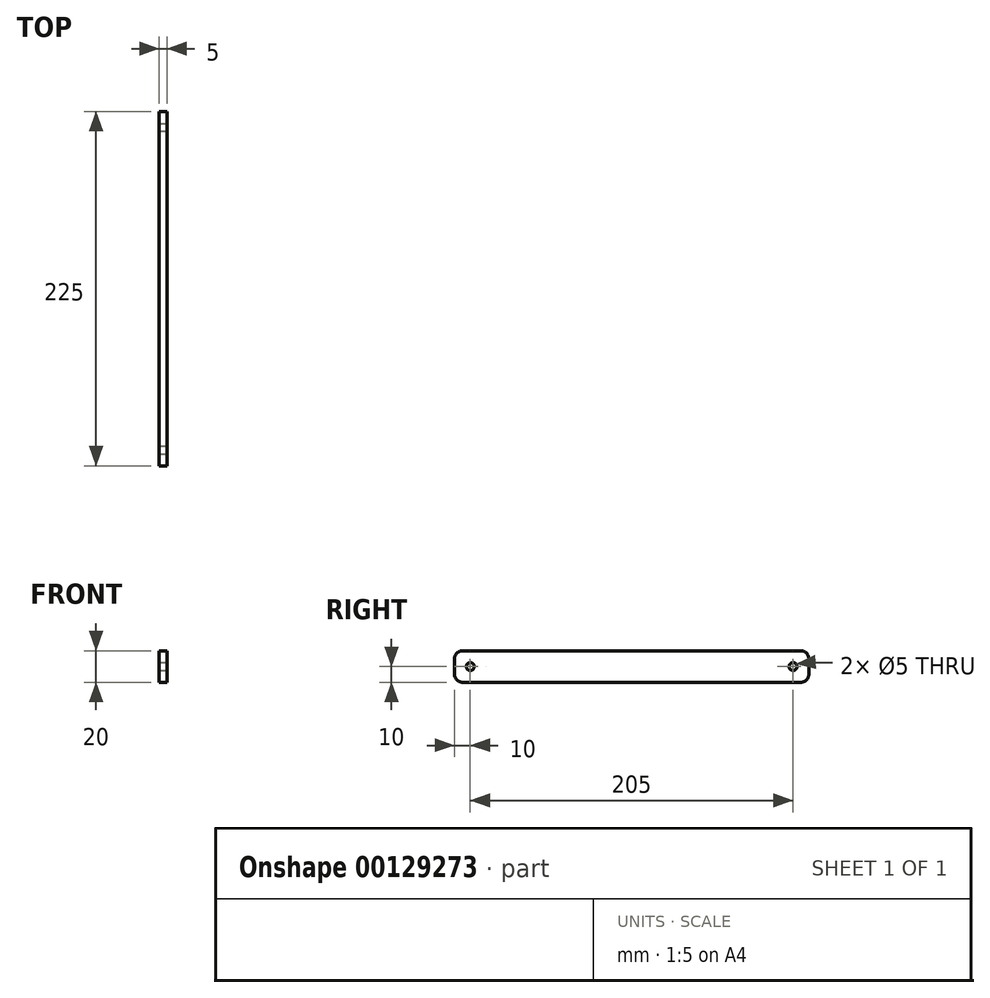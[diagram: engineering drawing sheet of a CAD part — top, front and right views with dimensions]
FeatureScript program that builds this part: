
annotation { "Feature Type Name" : "Feature", "Feature Type Description" : "" }
export const myFeature = defineFeature(function(context is Context, id is Id, definition is map)
    precondition{}
    {
        {
            var Q0;
            Q0=qCreatedBy(makeId("Right.planeOp"),FACE);
            var sketch = newSketch(context, id + "F0", { "sketchPlane" : qUnion([Q0])});
            skLineSegment(sketch, "E0.bottom", {"start": v(0, 0) * mm, "end": v(225, 0) * mm});
            skLineSegment(sketch, "E0.top", {"start": v(0, 20) * mm, "end": v(225, 20) * mm});
            skLineSegment(sketch, "E0.left", {"start": v(0, 0) * mm, "end": v(0, 20) * mm});
            skLineSegment(sketch, "E0.right", {"start": v(225, 0) * mm, "end": v(225, 20) * mm});
            skCircle(sketch, "E1", {"center": v(10, 10) * mm, "radius": 2.5 * mm});
            skPoint(sketch, "E1.centerSnap0", {"position": v(0, 10) * mm});
            skCircle(sketch, "E2", {"center": v(215, 10) * mm, "radius": 2.5 * mm});
            skSolve(sketch);
        }
        {
            var Q0;
            Q0=makeQuery(id+"F0.imprint","IMPRINT",FACE,{"disambiguationData":[TD([[makeQuery(id+"F0.imprint","IMPRINT",EDGE,{"derivedFrom":sQuery(id+"F0.wireOp",EDGE,"E0.bottom")}),1.0]])]});
            extrude(context, id + "F1", {"entities" : qUnion([Q0]), "oppositeDirection" : true, "depth" : 5 * mm});
        }
        {
            var Q0;
            Q0=makeQuery(id+"F1.opExtrude","SWEPT_EDGE",EDGE,{"disambiguationData":[OSD([sQuery(id+"F0.wireOp",EDGE,"E0.top"),sQuery(id+"F0.wireOp",EDGE,"E0.left")])]});
            var Q1;
            Q1=makeQuery(id+"F1.opExtrude","SWEPT_EDGE",EDGE,{"disambiguationData":[OSD([sQuery(id+"F0.wireOp",EDGE,"E0.bottom"),sQuery(id+"F0.wireOp",EDGE,"E0.left")])]});
            var Q2;
            Q2=makeQuery(id+"F1.opExtrude","SWEPT_EDGE",EDGE,{"disambiguationData":[OSD([sQuery(id+"F0.wireOp",EDGE,"E0.top"),sQuery(id+"F0.wireOp",EDGE,"E0.right")])]});
            var Q3;
            Q3=makeQuery(id+"F1.opExtrude","SWEPT_EDGE",EDGE,{"disambiguationData":[OSD([sQuery(id+"F0.wireOp",EDGE,"E0.bottom"),sQuery(id+"F0.wireOp",EDGE,"E0.right")])]});
            fillet(context, id + "F2", {"entities" : qUnion([Q0, Q1, Q2, Q3]), "radius" : 5 * mm, "tangentPropagation" : true, "allowEdgeOverflow" : false});
        }
    });
